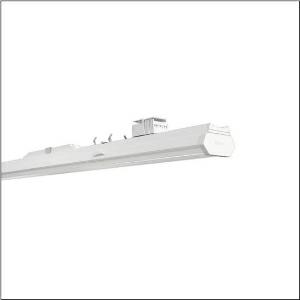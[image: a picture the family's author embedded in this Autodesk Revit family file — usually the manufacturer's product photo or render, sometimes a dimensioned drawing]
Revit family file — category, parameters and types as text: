
# Revit family: licross_r__11_protected_ho_51tp13cn4e5s_b79e
name_source: partatom
category: Lighting Fixtures
units: mm (PartAtom-declared; Revit-internal decimal feet)

## family parameters
Cut with Voids When Loaded = No
Host = Face
Light Source = No
Part Type = Normal
Room Calculation Point = No
Round Connector Dimension = Use Diameter
Shared = No

## types (1)
- --- (1 x LED, 14500 lm, 77.6 W, 4000K)
    Apparent Load = 78 VA
    CIE Flux Codes = 89 96 99 100 99
    Color Rendering = 80
    Color Temperature = 4000K
    Default Elevation = 1800 mm
    Description = Licross® 11 Protected HO, luminaire insert, of sheet steel, galvanised, coil coated, white, length: 1.500mm, width: 90mm, height: 101mm, LED rated luminous flux: 14.500lm, light colour: 840, control gear: ON/OFF Multilumen, CLOi, with plug, 3-pole, with phase selection, mains connection: 220..240V, AC, 50/60Hz, start of lifetime: 78W, end of service life: 87W, halogen-free wiring, primary light control with lens, of plastic, primary optical cover: cover, of PMMA, light emission: direct distribution, primary light characteristic: symmetric, protection rating (complete): IP64, insulation class (complete): insulation class I (protective earthing), certification: CE, ENEC, VDE, UKCA, protection symbol: D if used in an environment with conductive dust loads with corresponding accessories, impact resistance: IK06, permissible ambient temperature for indoor applications: -35..+35°C, corresponds to IFS (International Featured Standards) requirements for safety and quality in the food industry, reducing of maximum allowable ambient temperature of 5°C with ceiling mounting, LABS conformity tested according to VDMA 24364:2018-05, packaging unit: 1 piece
    Height = 92 mm
    Lamp = 1 x LED
    Lamp Light Flux = 14500 lm
    Lamp Power = 77.6 W
    Lamp count = 1
    Length = 1500 mm
    Luminous efficacy = 187 lm/W
    Manufacturer = Siteco
    ModVariant = No
    Model = 51TP13CN4E5S
    Mounting Place = Ceiling
    Mounting Type = Pendant
    Number of Poles = 1
    OnlyDefault = Yes
    Power Factor = 1
    Product Name = Licross® 11 Protected HO
    Product group = luminaire insert
    ProductGroupID = 902
    Protection Class = Protection class I
    Protection Degree = IP 64
    RLX_Detail_Level = 1
    RLX_Emergency_Light_Flux = 0 lm
    RLX_Emergency_Type = 0
    RLX_Emergency_Type_DB = No
    RlxData = <blob elided: 22033 chars, md5=0ce6674e>
    Socket = socket
    Standby Power = 0 W
    System Light Flux = 14500 lm
    System Power = 78 W
    Type Comments = factory setting: luminous flux: 100 % | (A | C | E) | 181 mA
    Type Image = l_1256148.jpg
    URL = http://relux.com
    VarID = @adj_085676
    Voltage = 0 V
    Weight = 0.00 kg
    Width = 88 mm

## geometry (parser evidence)
native form markers: Blend x4, Sweep x12
no freeform markers — native parametric forms only
